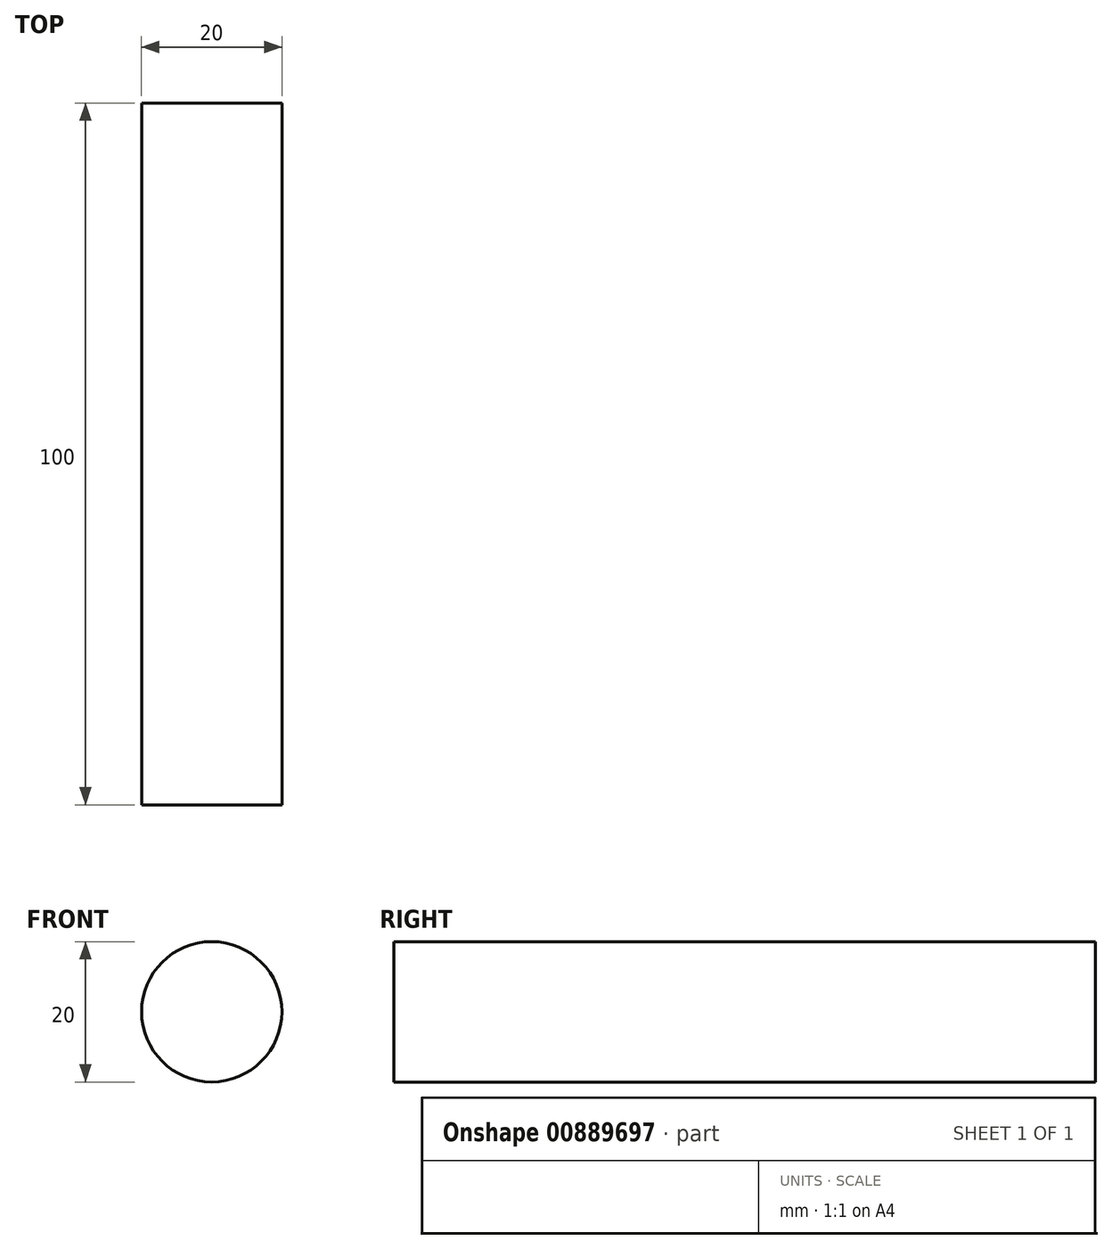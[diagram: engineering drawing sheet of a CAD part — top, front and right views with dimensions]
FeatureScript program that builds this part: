
annotation { "Feature Type Name" : "Feature", "Feature Type Description" : "" }
export const myFeature = defineFeature(function(context is Context, id is Id, definition is map)
    precondition{}
    {
        {
            var Q0;
            Q0=qCreatedBy(makeId("Front.planeOp"),FACE);
            var sketch = newSketch(context, id + "F1", { "sketchPlane" : qUnion([Q0])});
            skCircle(sketch, "E0", {"center": v(-40.37, 30.1) * mm, "radius": 10 * mm});
            skSolve(sketch);
        }
        {
            var Q0;
            Q0 = qSketchRegion(id + "F1", true);
            extrude(context, id + "F2", {"entities" : qUnion([Q0]), "depth" : 100 * mm, "offsetDistance" : 25.4 * mm});
        }
    });
